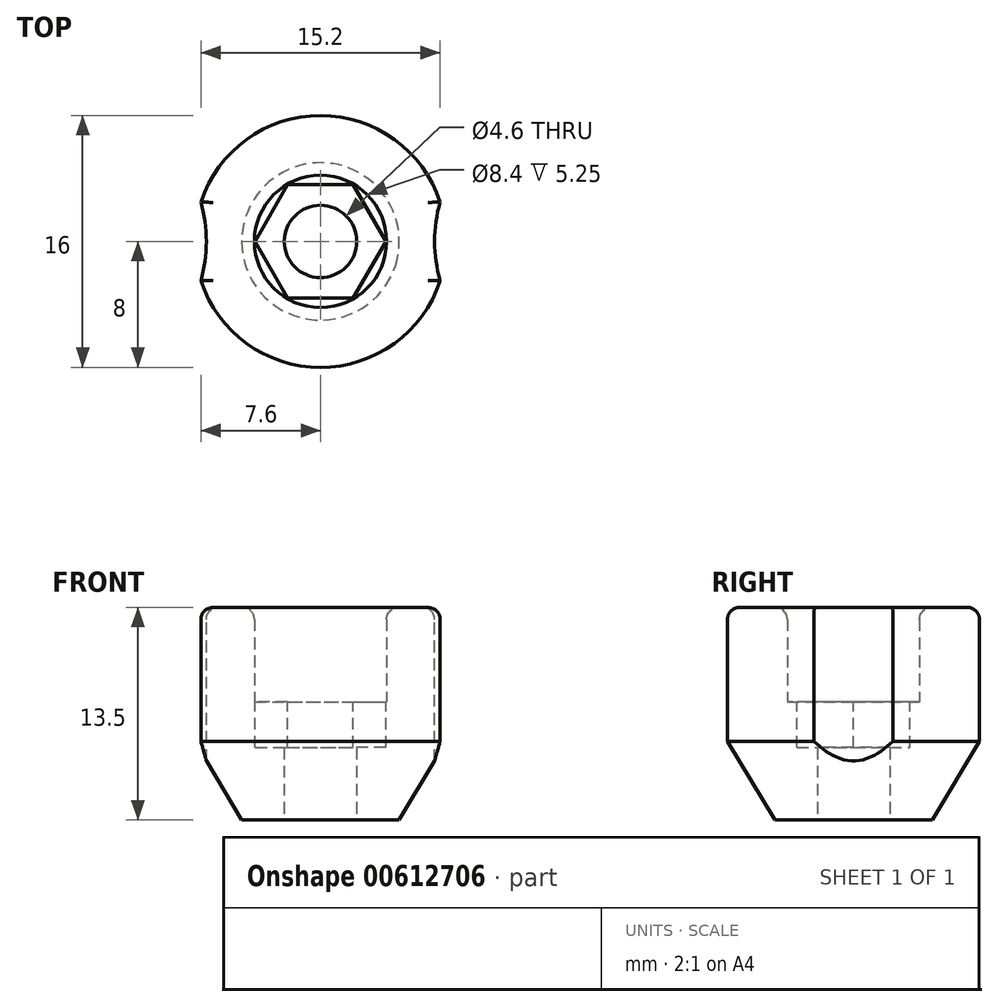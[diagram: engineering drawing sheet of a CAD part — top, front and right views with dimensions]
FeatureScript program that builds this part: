
annotation { "Feature Type Name" : "Feature", "Feature Type Description" : "" }
export const myFeature = defineFeature(function(context is Context, id is Id, definition is map)
    precondition{}
    {
        {
            var Q0;
            Q0=qCreatedBy(makeId("Front.planeOp"),FACE);
            var sketch = newSketch(context, id + "F0", { "sketchPlane" : qUnion([Q0])});
            skLineSegment(sketch, "E0", {"start": v(2.3, 0) * mm, "end": v(2.3, 7.5) * mm});
            skLineSegment(sketch, "E1", {"start": v(2.3, 7.5) * mm, "end": v(4.2, 7.5) * mm});
            skLineSegment(sketch, "E2", {"start": v(4.2, 7.5) * mm, "end": v(4.2, 13.5) * mm});
            skLineSegment(sketch, "E3", {"start": v(2.3, 0) * mm, "end": v(5, 0) * mm});
            skLineSegment(sketch, "E4", {"start": v(5, 0) * mm, "end": v(8, 5) * mm});
            skLineSegment(sketch, "E5", {"start": v(8, 5) * mm, "end": v(8, 13.5) * mm});
            skLineSegment(sketch, "E6", {"start": v(0, 0) * mm, "end": v(0, 16) * mm, "construction": true});
            skLineSegment(sketch, "E7", {"start": v(4.2, 13.5) * mm, "end": v(8, 13.5) * mm});
            skSolve(sketch);
        }
        {
            var Q0;
            Q0=makeQuery(id+"F0.imprint","IMPRINT",FACE,{"disambiguationData":[TD([[makeQuery(id+"F0.imprint","IMPRINT",EDGE,{"derivedFrom":sQuery(id+"F0.wireOp",EDGE,"E0")}),-1.0]])]});
            var Q1;
            Q1=sQuery(id+"F0.wireOp",EDGE,"E6");
            revolve(context, id + "F1", {"entities" : qUnion([Q0]), "axis" : qUnion([Q1]), "revolveType" : RevolveType.FULL});
        }
        {
            var Q0;
            Q0=makeQuery(id+"F1.opRevolve","SWEPT_FACE",FACE,{"disambiguationData":[OSD([sQuery(id+"F0.wireOp",EDGE,"E1")])]});
            var sketch = newSketch(context, id + "F2", { "sketchPlane" : qUnion([Q0])});
            skCircle(sketch, "E8.cCircle", {"center": v(0, 0) * mm, "radius": 3.6 * mm, "construction": true});
            skLineSegment(sketch, "E8.0", {"start": v(-2.08, 3.6) * mm, "end": v(2.08, 3.6) * mm});
            skLineSegment(sketch, "E8.1", {"start": v(2.08, 3.6) * mm, "end": v(4.16, 0) * mm});
            skLineSegment(sketch, "E8.2", {"start": v(4.16, 0) * mm, "end": v(2.08, -3.6) * mm});
            skLineSegment(sketch, "E8.3", {"start": v(2.08, -3.6) * mm, "end": v(-2.08, -3.6) * mm});
            skLineSegment(sketch, "E8.4", {"start": v(-2.08, -3.6) * mm, "end": v(-4.16, 0) * mm});
            skLineSegment(sketch, "E8.5", {"start": v(-4.16, 0) * mm, "end": v(-2.08, 3.6) * mm});
            skPoint(sketch, "E8.0.midPoint", {"position": v(0, 3.6) * mm});
            skSolve(sketch);
        }
        {
            var Q0;
            Q0=makeQuery(id+"F2.imprint","IMPRINT",FACE,{"disambiguationData":[TD([[makeQuery(id+"F2.imprint","IMPRINT",EDGE,{"derivedFrom":sQuery(id+"F2.wireOp",EDGE,"E8.0")}),-1.0]])]});
            extrude(context, id + "F3", {"entities" : qUnion([Q0]), "operationType" : NewBodyOperationType.REMOVE, "oppositeDirection" : true, "depth" : 2.9 * mm});
        }
        {
            var Q0;
            Q0=makeQuery(id+"F1.opRevolve","SWEPT_FACE",FACE,{"disambiguationData":[OSD([sQuery(id+"F0.wireOp",EDGE,"E7")])]});
            var sketch = newSketch(context, id + "F4", { "sketchPlane" : qUnion([Q0])});
            skCircle(sketch, "E9", {"center": v(16.37, 0) * mm, "radius": 9.12 * mm});
            skCircle(sketch, "E10", {"center": v(-16.37, 0) * mm, "radius": 9.12 * mm});
            skLineSegment(sketch, "E11", {"start": v(-7.25, 0) * mm, "end": v(0, 0) * mm, "construction": true});
            skLineSegment(sketch, "E12", {"start": v(0, 0) * mm, "end": v(7.25, 0) * mm, "construction": true});
            skLineSegment(sketch, "E13", {"start": v(7.6, 2.5) * mm, "end": v(7.6, -2.5) * mm, "construction": true});
            skSolve(sketch);
        }
        {
            var Q0;
            {var subQ0=sQuery(id+"F4.wireOp",EDGE,"E10");var subQ1=makeQuery(id+"F1.opRevolve","SWEPT_EDGE",EDGE,{"disambiguationData":[OSD([sQuery(id+"F0.wireOp",EDGE,"E5"),sQuery(id+"F0.wireOp",EDGE,"E7")])]});var subQ2=makeQuery(id+"F4.imprint","INTERSECT",VERTEX,{"disambiguationData":[OD(0.0)],"derivedFrom":[subQ1,subQ0]});Q0=makeQuery(id+"F4.imprint","IMPRINT",FACE,{"disambiguationData":[TD([[makeQuery(id+"F4.imprint","IMPRINT",EDGE,{"disambiguationData":[TD([[subQ2,-1.0]])],"derivedFrom":subQ0}),1.0]])]});}
            var Q1;
            {var subQ0=sQuery(id+"F4.wireOp",EDGE,"E9");var subQ1=makeQuery(id+"F1.opRevolve","SWEPT_EDGE",EDGE,{"disambiguationData":[OSD([sQuery(id+"F0.wireOp",EDGE,"E5"),sQuery(id+"F0.wireOp",EDGE,"E7")])]});var subQ2=makeQuery(id+"F4.imprint","INTERSECT",VERTEX,{"disambiguationData":[OD(0.0)],"derivedFrom":[subQ1,subQ0]});Q1=makeQuery(id+"F4.imprint","IMPRINT",FACE,{"disambiguationData":[TD([[makeQuery(id+"F4.imprint","IMPRINT",EDGE,{"disambiguationData":[TD([[subQ2,1.0]])],"derivedFrom":subQ0}),1.0]])]});}
            extrude(context, id + "F5", {"entities" : qUnion([Q0, Q1]), "operationType" : NewBodyOperationType.REMOVE, "endBound" : BoundingType.THROUGH_ALL, "oppositeDirection" : true, "depth" : 25 * mm});
        }
        {
            var Q0;
            Q0=makeQuery(id+"F1.opRevolve","SWEPT_FACE",FACE,{"disambiguationData":[OSD([sQuery(id+"F0.wireOp",EDGE,"E7")])]});
            fillet(context, id + "F6", {"entities" : qUnion([Q0]), "radius" : 0.75 * mm, "tangentPropagation" : true, "allowEdgeOverflow" : false});
        }
    });
